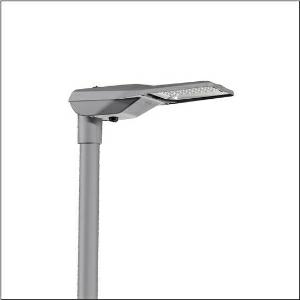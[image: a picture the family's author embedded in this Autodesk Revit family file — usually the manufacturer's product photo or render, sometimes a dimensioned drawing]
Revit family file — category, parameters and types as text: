
# Revit family: streetlight_sl_21_iq_mini___st1_0ab_5xe2m31y08hb_576a
name_source: partatom
category: Lighting Fixtures
units: mm (PartAtom-declared; Revit-internal decimal feet)

## family parameters
Cut with Voids When Loaded = No
Host = Face
Light Source = No
Part Type = Normal
Room Calculation Point = No
Round Connector Dimension = Use Diameter
Shared = No

## types (1)
- --- (1 x LED, 8580 lm, 71 W, 3000K)
    Apparent Load = 71 VA
    CIE Flux Codes = 38 73 97 100 100
    Color Rendering = 70
    Color Temperature = 3000K
    Default Elevation = 1800 mm
    Description = Streetlight SL 21 iQ mini, mast luminaire, primary light control with lens, of PMMA, primary optical cover: cover, of toughened safety glass, transparent, light distribution: ST1.0aB, light emission: direct distribution, primary light characteristic: asymmetric, installation type: post-top, side-entry, LED, High Power LED, rated luminous flux: 8.580lm, luminous efficacy: 121lm/W, light colour: 730, colour temperature: 3000K, control gear: iQ-Street Remote, D4i with power reduction, control: pre-setting: logarithmic dimming characteristic, Street-Remote, Auto-Match, Temp-Guard, Lumen-Switch, Night-Set, Smart-Wire, Light-Fading, Desk-Remote (wireless, voltage-free reading and setting of iQ features in the workshop via application-optimized NFC function/RFID function), optimised constant luminous flux control (CLO 2.0), mains connection: 220..240V, AC, 50/60Hz, start of lifetime: 71W, end of service life: 75W, reduction: 30W, luminaire housing, of diecast aluminium, powder-coated, Siteco® metallic grey (DB 702S), corrosivity category C5 mid according to DIN EN ISO 12944, please order mast flange separately, inclination adjustable: 0°, 5°, 10°, 15°, sealing non-destructively replaceable, multi-level sealing system, length: 628mm, width: 235mm, height: 110mm, mast flange for spigot size: 42mm (side-entry): 5XC10008XM4, 60/48mm (side-entry/post-top): 5XC10108XM2, 76/60mm (side-entry/post-top): 5XC10108XM1, mounting height: 4..8m, Smart Interface below and above, protection rating (complete): IP66, insulation class (complete): insulation class II (safety insulation), certification: CE, ENEC, ENEC+, VDE, impact resistance: IK10, permissible operating ambient temperature for outdoor applications: -40..+50°C, standard-compliant lighting for roads and squares, packaging unit: 1 piece

Light Distribution: ST1.0aB
    Height = 110 mm
    Lamp = 1 x LED
    Lamp Light Flux = 8580 lm
    Lamp Power = 71 W
    Lamp count = 1
    Length = 625 mm
    Luminous efficacy = 121 lm/W
    Manufacturer = Siteco
    ModVariant = No
    Model = 5XE2M31Y08HB
    Number of Poles = 1
    OnlyDefault = Yes
    Power Factor = 1
    Product Name = Streetlight SL 21 iQ mini | ST1.0aB
    Product group = mast luminaire | pylon top
    ProductGroupID = 6100
    Protection Class = Protection class II
    Protection Degree = IP 66
    RLX_Detail_Level = 1
    RLX_Emergency_Light_Flux = 0 lm
    RLX_Emergency_Type = 0
    RLX_Emergency_Type_DB = No
    RlxData = <blob elided: 92801 chars, md5=ba8a559b>
    Socket = socket
    Standby Power = 0 W
    System Light Flux = 8580 lm
    System Power = 71 W
    Type Comments = factory setting: luminous flux: 100 % | dim-lin: 254 | 716 mA
    Type Image = l_1003514.jpg
    URL = http://relux.com
    VarID = @adj_133877
    Voltage = 0 V
    Weight = 0.00 kg
    Width = 234 mm

## geometry (parser evidence)
native form markers: Blend x4, Sweep x10
no freeform markers — native parametric forms only
